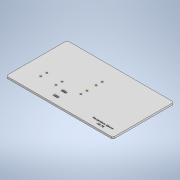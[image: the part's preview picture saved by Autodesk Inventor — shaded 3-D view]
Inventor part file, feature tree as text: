
AUTODESK INVENTOR PART (.ipt)
format: ipt  version: 2022 (Build 260153000, 153)  size: 146,944 bytes
history: native  units: mm
features: sketch x3, extrude x2, fillet x1, hole x1
ambient origin geometry x8: Origin, YZ Plane, XZ Plane, XY Plane, X Axis, Y Axis, Z Axis, Center Point
bodies: Solid1 (feature_tree)
feature tree (7):
  extrude  "Extrusion1"  Depth=200.0mm
  fillet  "Fillet1"  Radius=6.0mm
  sketch  "Sketch2"  dims[d4=5.0mm d7=20.0mm]
  sketch  "Sketch3"  dims[d8=20.0mm d11=5.4mm d12=6.0mm d13=4.0mm d14=2.0mm d15=90.0deg d16=8.0mm d17=20.594885mm d18=20.0mm d19=20.0mm d20=50.0mm d21=58.5mm d22=55.0mm d23=60.0mm d24=30.0mm d25=15.0mm d26=6.0mm d27=35.0mm d28=0.0mm d29=0.0mm d30=50.0mm d31=15.0mm d32=6.0mm d33=35.0mm d34=20.0mm]
  hole  "Hole1"  [1 undecoded]
  extrude  "Extrusion2"  Depth=20.0mm
  sketch  "Sketch1"  dims[d0=350.0mm d1=200.0mm d2=6.0mm d3=0.0mm]
note: 1 required parameter value undecoded (feature->parameter linkage not recoverable at this tier; creation-order binding heuristic only, values carry confidence <= 0.55)
